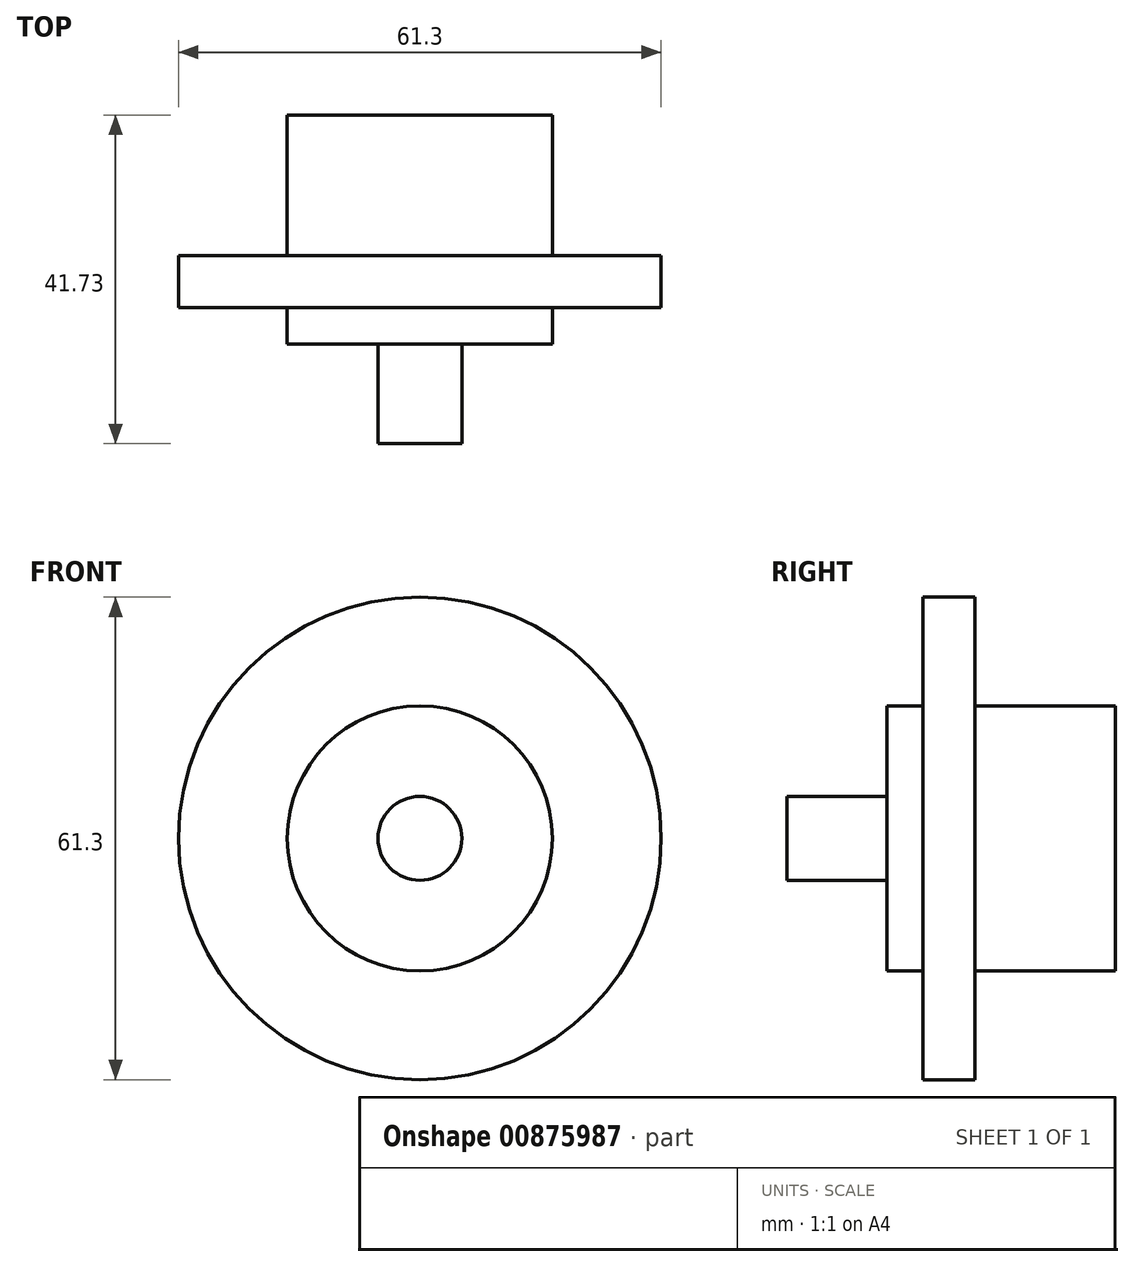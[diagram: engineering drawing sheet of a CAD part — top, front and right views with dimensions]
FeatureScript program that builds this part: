
annotation { "Feature Type Name" : "Feature", "Feature Type Description" : "" }
export const myFeature = defineFeature(function(context is Context, id is Id, definition is map)
    precondition{}
    {
        {
            var Q0;
            Q0=qCreatedBy(makeId("Right.planeOp"),FACE);
            var sketch = newSketch(context, id + "F0", { "sketchPlane" : qUnion([Q0])});
            skLineSegment(sketch, "E0", {"start": v(-20, 0) * mm, "end": v(-20, 5.32) * mm});
            skLineSegment(sketch, "E1", {"start": v(-20, 5.32) * mm, "end": v(-7.34, 5.32) * mm});
            skLineSegment(sketch, "E2", {"start": v(-7.34, 5.32) * mm, "end": v(-7.34, 16.84) * mm});
            skLineSegment(sketch, "E3", {"start": v(-7.34, 16.84) * mm, "end": v(-2.73, 16.84) * mm});
            skLineSegment(sketch, "E4", {"start": v(-2.73, 16.84) * mm, "end": v(-2.73, 30.65) * mm});
            skLineSegment(sketch, "E5", {"start": v(-2.73, 30.65) * mm, "end": v(0, 30.65) * mm});
            skLineSegment(sketch, "E6", {"start": v(0, 30.65) * mm, "end": v(3.89, 30.65) * mm});
            skLineSegment(sketch, "E7", {"start": v(3.89, 30.65) * mm, "end": v(3.89, 16.84) * mm});
            skLineSegment(sketch, "E8", {"start": v(3.89, 16.84) * mm, "end": v(21.73, 16.84) * mm});
            skLineSegment(sketch, "E9", {"start": v(21.73, 16.84) * mm, "end": v(21.73, 0) * mm});
            skLineSegment(sketch, "E10", {"start": v(21.73, 0) * mm, "end": v(-20, 0) * mm});
            skSolve(sketch);
        }
        {
            var Q0;
            Q0=makeQuery(id+"F0.imprint","IMPRINT",FACE,{"disambiguationData":[TD([[makeQuery(id+"F0.imprint","IMPRINT",EDGE,{"derivedFrom":sQuery(id+"F0.wireOp",EDGE,"E0")}),-1.0]])]});
            var Q1;
            Q1=sQuery(id+"F0.wireOp",EDGE,"E10");
            revolve(context, id + "F1", {"surfaceOperationType" : NewSurfaceOperationType.NEW, "entities" : qUnion([Q0]), "axis" : qUnion([Q1]), "revolveType" : RevolveType.FULL});
        }
    });
